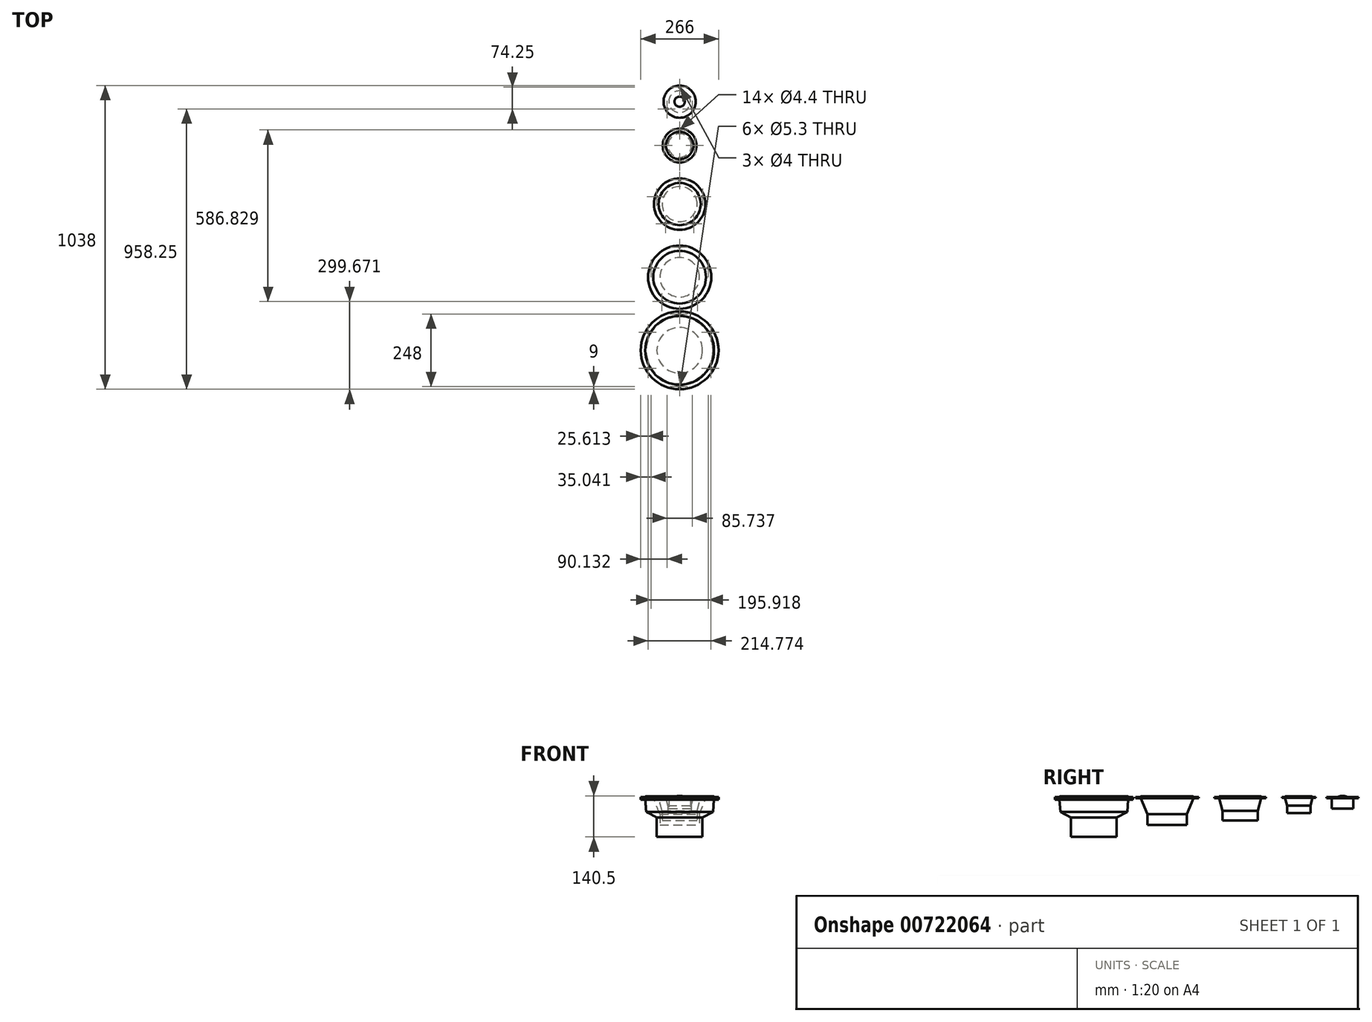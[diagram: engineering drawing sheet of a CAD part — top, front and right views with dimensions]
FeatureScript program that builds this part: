
annotation { "Feature Type Name" : "Feature", "Feature Type Description" : "" }
export const myFeature = defineFeature(function(context is Context, id is Id, definition is map)
    precondition{}
    {
        {
            var Q0;
            Q0=qCreatedBy(makeId("Front.planeOp"),FACE);
            cPlane(context, id + "F0", {"entities" : qUnion([Q0]), "cplaneType" : CPlaneType.OFFSET, "offset" : 150 * mm, "width" : 150 * mm, "height" : 150 * mm});
        }
        {
            var Q0;
            Q0=qCreatedBy(id+"F0.planeOp",FACE);
            cPlane(context, id + "F1", {"entities" : qUnion([Q0]), "cplaneType" : CPlaneType.OFFSET, "offset" : 200 * mm, "width" : 150 * mm, "height" : 150 * mm});
        }
        {
            var Q0;
            Q0=qCreatedBy(id+"F1.planeOp",FACE);
            cPlane(context, id + "F2", {"entities" : qUnion([Q0]), "cplaneType" : CPlaneType.OFFSET, "offset" : 250 * mm, "width" : 150 * mm, "height" : 150 * mm});
        }
        {
            var Q0;
            Q0=qCreatedBy(id+"F2.planeOp",FACE);
            cPlane(context, id + "F3", {"entities" : qUnion([Q0]), "cplaneType" : CPlaneType.OFFSET, "offset" : 250 * mm, "width" : 150 * mm, "height" : 150 * mm});
        }
        {
            var Q0;
            Q0=qCreatedBy(makeId("Front.planeOp"),FACE);
            var sketch = newSketch(context, id + "F4", { "sketchPlane" : qUnion([Q0])});
            skLineSegment(sketch, "E0", {"start": v(-17.5, 0) * mm, "end": v(-55, 0) * mm});
            skLineSegment(sketch, "E1", {"start": v(-55, 0) * mm, "end": v(-55, -4) * mm});
            skLineSegment(sketch, "E2", {"start": v(-55, -4) * mm, "end": v(-37, -4) * mm});
            skLineSegment(sketch, "E3", {"start": v(-37, -4) * mm, "end": v(-37, -40) * mm});
            skLineSegment(sketch, "E4", {"start": v(-37, -40) * mm, "end": v(0, -40) * mm});
            skLineSegment(sketch, "E5", {"start": v(0, -40) * mm, "end": v(0, 0) * mm});
            skArc(sketch, "E6", {"start": v(0, 4) * mm, "mid": v(-8.98, 2.99) * mm, "end": v(-17.5, 0) * mm});
            skLineSegment(sketch, "E7", {"start": v(0, 0) * mm, "end": v(0, 4) * mm});
            skSolve(sketch);
        }
        {
            var Q0;
            Q0 = qSketchRegion(id + "F4", true);
            var Q1;
            Q1=sQuery(id+"F4.wireOp",EDGE,"E5");
            revolve(context, id + "F5", {"surfaceOperationType" : NewSurfaceOperationType.NEW, "entities" : qUnion([Q0]), "axis" : qUnion([Q1]), "revolveType" : RevolveType.FULL});
        }
        {
            var Q0;
            Q0=makeQuery(id+"F5.opRevolve","SWEPT_FACE",FACE,{"disambiguationData":[OSD([sQuery(id+"F4.wireOp",EDGE,"E0")])]});
            var sketch = newSketch(context, id + "F6", { "sketchPlane" : qUnion([Q0])});
            skCircle(sketch, "E8", {"center": v(0, 49.5) * mm, "radius": 2 * mm});
            skCircle(sketch, "E9.1.0", {"center": v(-42.87, -24.75) * mm, "radius": 2 * mm});
            skCircle(sketch, "E9.2.0", {"center": v(42.87, -24.75) * mm, "radius": 2 * mm});
            skPoint(sketch, "E9.center", {"position": v(0, 0) * mm});
            skSolve(sketch);
        }
        {
            var Q0;
            Q0 = qSketchRegion(id + "F6", true);
            extrude(context, id + "F7", {"entities" : qUnion([Q0]), "operationType" : NewBodyOperationType.REMOVE, "endBound" : BoundingType.UP_TO_NEXT, "oppositeDirection" : true, "depth" : 25 * mm, "offsetDistance" : 25 * mm});
        }
        {
            var Q0;
            Q0=qCreatedBy(id+"F0.planeOp",FACE);
            var sketch = newSketch(context, id + "F8", { "sketchPlane" : qUnion([Q0])});
            skLineSegment(sketch, "E10", {"start": v(0, 3) * mm, "end": v(-43.8, 3) * mm});
            skLineSegment(sketch, "E11", {"start": v(-46.8, 0) * mm, "end": v(-46.8, 0) * mm});
            skLineSegment(sketch, "E12", {"start": v(-46.8, 0) * mm, "end": v(-57.8, 0) * mm});
            skLineSegment(sketch, "E13", {"start": v(-57.8, 0) * mm, "end": v(-57.8, -2.8) * mm});
            skLineSegment(sketch, "E14", {"start": v(-57.8, -2.8) * mm, "end": v(-46.8, -2.8) * mm});
            skLineSegment(sketch, "E15", {"start": v(-46.8, -2.8) * mm, "end": v(-40, -29.7) * mm});
            skLineSegment(sketch, "E16", {"start": v(-40, -29.7) * mm, "end": v(-40, -54.7) * mm});
            skLineSegment(sketch, "E17", {"start": v(-40, -54.7) * mm, "end": v(0, -54.7) * mm});
            skLineSegment(sketch, "E18", {"start": v(0, -54.7) * mm, "end": v(0, 3) * mm});
            skPoint(sketch, "E19.visualSharp", {"position": v(-46.8, 3) * mm});
            skArc(sketch, "E19.filletArc", {"start": v(-43.8, 3) * mm, "mid": v(-45.92, 2.12) * mm, "end": v(-46.8, 0) * mm});
            skSolve(sketch);
        }
        {
            var Q0;
            Q0 = qSketchRegion(id + "F8", true);
            var Q1;
            Q1=sQuery(id+"F8.wireOp",EDGE,"E18");
            revolve(context, id + "F9", {"surfaceOperationType" : NewSurfaceOperationType.NEW, "entities" : qUnion([Q0]), "axis" : qUnion([Q1]), "revolveType" : RevolveType.FULL});
        }
        {
            var Q0;
            Q0=makeQuery(id+"F9.opRevolve","SWEPT_FACE",FACE,{"disambiguationData":[OSD([sQuery(id+"F8.wireOp",EDGE,"E12")])]});
            var sketch = newSketch(context, id + "F10", { "sketchPlane" : qUnion([Q0])});
            skCircle(sketch, "E20", {"center": v(0, -96.5) * mm, "radius": 2.2 * mm});
            skCircle(sketch, "E21.1.0", {"center": v(-53.5, -150) * mm, "radius": 2.2 * mm});
            skCircle(sketch, "E21.2.0", {"center": v(0, -203.5) * mm, "radius": 2.2 * mm});
            skCircle(sketch, "E21.3.0", {"center": v(53.5, -150) * mm, "radius": 2.2 * mm});
            skPoint(sketch, "E21.center", {"position": v(0, -150) * mm});
            skSolve(sketch);
        }
        {
            var Q0;
            Q0 = qSketchRegion(id + "F10", true);
            extrude(context, id + "F11", {"entities" : qUnion([Q0]), "operationType" : NewBodyOperationType.REMOVE, "endBound" : BoundingType.UP_TO_NEXT, "oppositeDirection" : true, "depth" : 25 * mm, "offsetDistance" : 25 * mm});
        }
        {
            var Q0;
            Q0=qCreatedBy(id+"F1.planeOp",FACE);
            var sketch = newSketch(context, id + "F12", { "sketchPlane" : qUnion([Q0])});
            skLineSegment(sketch, "E22", {"start": v(0, 3) * mm, "end": v(-69, 3) * mm});
            skLineSegment(sketch, "E23", {"start": v(-72, 0) * mm, "end": v(-72, 0) * mm});
            skLineSegment(sketch, "E24", {"start": v(-72, 0) * mm, "end": v(-87.8, 0) * mm});
            skLineSegment(sketch, "E25", {"start": v(-87.8, 0) * mm, "end": v(-87.8, -3.5) * mm});
            skLineSegment(sketch, "E26", {"start": v(-87.8, -3.5) * mm, "end": v(-72, -3.5) * mm});
            skLineSegment(sketch, "E27", {"start": v(-72, -3.5) * mm, "end": v(-60, -47.1) * mm});
            skLineSegment(sketch, "E28", {"start": v(-60, -47.1) * mm, "end": v(-60, -80.6) * mm});
            skLineSegment(sketch, "E29", {"start": v(-60, -80.6) * mm, "end": v(0, -80.6) * mm});
            skLineSegment(sketch, "E30", {"start": v(0, -80.6) * mm, "end": v(0, 3) * mm});
            skPoint(sketch, "E31.visualSharp", {"position": v(-72, 3) * mm});
            skArc(sketch, "E31.filletArc", {"start": v(-69, 3) * mm, "mid": v(-71.12, 2.12) * mm, "end": v(-72, 0) * mm});
            skSolve(sketch);
        }
        {
            var Q0;
            Q0 = qSketchRegion(id + "F12", true);
            var Q1;
            Q1=sQuery(id+"F12.wireOp",EDGE,"E30");
            revolve(context, id + "F13", {"surfaceOperationType" : NewSurfaceOperationType.NEW, "entities" : qUnion([Q0]), "axis" : qUnion([Q1]), "revolveType" : RevolveType.FULL});
        }
        {
            var Q0;
            Q0=makeQuery(id+"F13.opRevolve","SWEPT_FACE",FACE,{"disambiguationData":[OSD([sQuery(id+"F12.wireOp",EDGE,"E24")])]});
            var sketch = newSketch(context, id + "F14", { "sketchPlane" : qUnion([Q0])});
            skCircle(sketch, "E32", {"center": v(0, -267) * mm, "radius": 2.2 * mm});
            skCircle(sketch, "E33.1.0", {"center": v(-78.94, -324.35) * mm, "radius": 2.2 * mm});
            skCircle(sketch, "E33.2.0", {"center": v(-48.79, -417.15) * mm, "radius": 2.2 * mm});
            skCircle(sketch, "E33.3.0", {"center": v(48.79, -417.15) * mm, "radius": 2.2 * mm});
            skCircle(sketch, "E33.4.0", {"center": v(78.94, -324.35) * mm, "radius": 2.2 * mm});
            skPoint(sketch, "E33.center", {"position": v(0, -350) * mm});
            skSolve(sketch);
        }
        {
            var Q0;
            Q0 = qSketchRegion(id + "F14", true);
            extrude(context, id + "F15", {"entities" : qUnion([Q0]), "operationType" : NewBodyOperationType.REMOVE, "endBound" : BoundingType.UP_TO_NEXT, "oppositeDirection" : true, "depth" : 25 * mm, "offsetDistance" : 25 * mm});
        }
        {
            var Q0;
            Q0=qCreatedBy(id+"F2.planeOp",FACE);
            var sketch = newSketch(context, id + "F16", { "sketchPlane" : qUnion([Q0])});
            skLineSegment(sketch, "E34", {"start": v(0, 3) * mm, "end": v(-87, 3) * mm});
            skLineSegment(sketch, "E35", {"start": v(-90, 0) * mm, "end": v(-90, 0) * mm});
            skLineSegment(sketch, "E36", {"start": v(-90, 0) * mm, "end": v(-108, 0) * mm});
            skLineSegment(sketch, "E37", {"start": v(-108, 0) * mm, "end": v(-108, -3.5) * mm});
            skLineSegment(sketch, "E38", {"start": v(-108, -3.5) * mm, "end": v(-90, -3.5) * mm});
            skLineSegment(sketch, "E39", {"start": v(-90, -3.5) * mm, "end": v(-67.5, -58.5) * mm});
            skLineSegment(sketch, "E40", {"start": v(-67.5, -58.5) * mm, "end": v(-67.5, -95.5) * mm});
            skLineSegment(sketch, "E41", {"start": v(-67.5, -95.5) * mm, "end": v(0, -95.5) * mm});
            skLineSegment(sketch, "E42", {"start": v(0, -95.5) * mm, "end": v(0, 3) * mm});
            skPoint(sketch, "E43.visualSharp", {"position": v(-90, 3) * mm});
            skArc(sketch, "E43.filletArc", {"start": v(-87, 3) * mm, "mid": v(-89.12, 2.12) * mm, "end": v(-90, 0) * mm});
            skSolve(sketch);
        }
        {
            var Q0;
            Q0 = qSketchRegion(id + "F16", true);
            var Q1;
            Q1=sQuery(id+"F16.wireOp",EDGE,"E42");
            revolve(context, id + "F17", {"surfaceOperationType" : NewSurfaceOperationType.NEW, "entities" : qUnion([Q0]), "axis" : qUnion([Q1]), "revolveType" : RevolveType.FULL});
        }
        {
            var Q0;
            Q0=makeQuery(id+"F17.opRevolve","SWEPT_FACE",FACE,{"disambiguationData":[OSD([sQuery(id+"F16.wireOp",EDGE,"E36")])]});
            var sketch = newSketch(context, id + "F18", { "sketchPlane" : qUnion([Q0])});
            skCircle(sketch, "E44", {"center": v(0, -497) * mm, "radius": 2.2 * mm});
            skCircle(sketch, "E45.1.0", {"center": v(-97.96, -568.17) * mm, "radius": 2.2 * mm});
            skCircle(sketch, "E45.2.0", {"center": v(-60.54, -683.33) * mm, "radius": 2.2 * mm});
            skCircle(sketch, "E45.3.0", {"center": v(60.54, -683.33) * mm, "radius": 2.2 * mm});
            skCircle(sketch, "E45.4.0", {"center": v(97.96, -568.17) * mm, "radius": 2.2 * mm});
            skPoint(sketch, "E45.center", {"position": v(0, -600) * mm});
            skSolve(sketch);
        }
        {
            var Q0;
            Q0 = qSketchRegion(id + "F18", true);
            extrude(context, id + "F19", {"entities" : qUnion([Q0]), "operationType" : NewBodyOperationType.REMOVE, "endBound" : BoundingType.UP_TO_NEXT, "oppositeDirection" : true, "depth" : 25 * mm, "offsetDistance" : 25 * mm});
        }
        {
            var Q0;
            Q0=qCreatedBy(id+"F3.planeOp",FACE);
            var sketch = newSketch(context, id + "F20", { "sketchPlane" : qUnion([Q0])});
            skLineSegment(sketch, "E46", {"start": v(0, 3) * mm, "end": v(-114.5, 3) * mm});
            skLineSegment(sketch, "E47", {"start": v(-117.5, 0) * mm, "end": v(-117.5, 0) * mm});
            skLineSegment(sketch, "E48", {"start": v(-117.5, 0) * mm, "end": v(-133, 0) * mm});
            skLineSegment(sketch, "E49", {"start": v(-133, 0) * mm, "end": v(-133, -9.5) * mm});
            skLineSegment(sketch, "E50", {"start": v(-133, -9.5) * mm, "end": v(-117.5, -9.5) * mm});
            skLineSegment(sketch, "E51", {"start": v(-78, -70) * mm, "end": v(-78, -136.5) * mm});
            skLineSegment(sketch, "E52", {"start": v(-78, -136.5) * mm, "end": v(0, -136.5) * mm});
            skLineSegment(sketch, "E53", {"start": v(0, -136.5) * mm, "end": v(0, 3) * mm});
            skPoint(sketch, "E54.visualSharp", {"position": v(-117.5, 3) * mm});
            skArc(sketch, "E54.filletArc", {"start": v(-114.5, 3) * mm, "mid": v(-116.62, 2.12) * mm, "end": v(-117.5, 0) * mm});
            skLineSegment(sketch, "E55", {"start": v(-117.5, -9.5) * mm, "end": v(-114.32, -50.7) * mm});
            skLineSegment(sketch, "E56", {"start": v(-114.32, -50.7) * mm, "end": v(-78, -70) * mm});
            skSolve(sketch);
        }
        {
            var Q0;
            Q0 = qSketchRegion(id + "F20", true);
            var Q1;
            Q1=sQuery(id+"F20.wireOp",EDGE,"E53");
            revolve(context, id + "F21", {"surfaceOperationType" : NewSurfaceOperationType.NEW, "entities" : qUnion([Q0]), "axis" : qUnion([Q1]), "revolveType" : RevolveType.FULL});
        }
        {
            var Q0;
            Q0=makeQuery(id+"F21.opRevolve","SWEPT_FACE",FACE,{"disambiguationData":[OSD([sQuery(id+"F20.wireOp",EDGE,"E48")])]});
            var sketch = newSketch(context, id + "F22", { "sketchPlane" : qUnion([Q0])});
            skCircle(sketch, "E57", {"center": v(0, -726) * mm, "radius": 2.65 * mm});
            skCircle(sketch, "E58.1.0", {"center": v(-107.39, -788) * mm, "radius": 2.65 * mm});
            skCircle(sketch, "E58.2.0", {"center": v(-107.39, -912) * mm, "radius": 2.65 * mm});
            skCircle(sketch, "E58.3.0", {"center": v(0, -974) * mm, "radius": 2.65 * mm});
            skCircle(sketch, "E58.4.0", {"center": v(107.39, -912) * mm, "radius": 2.65 * mm});
            skCircle(sketch, "E58.5.0", {"center": v(107.39, -788) * mm, "radius": 2.65 * mm});
            skPoint(sketch, "E58.center", {"position": v(0, -850) * mm});
            skSolve(sketch);
        }
        {
            var Q0;
            Q0 = qSketchRegion(id + "F22", true);
            extrude(context, id + "F23", {"entities" : qUnion([Q0]), "operationType" : NewBodyOperationType.REMOVE, "endBound" : BoundingType.UP_TO_NEXT, "oppositeDirection" : true, "depth" : 25 * mm, "offsetDistance" : 25 * mm});
        }
    });
